# Revit family: NLRS_57_DUF_UN_round-tee-piece_LT_velu
name_source: partatom
category: Duct Fittings
units: mm (PartAtom-declared; Revit-internal decimal feet)

## family parameters
Always vertical = Yes
Cut with Voids When Loaded = No
OmniClass Number = 23.75.70.14.14
OmniClass Title = Couplings for Air Ductwork
Part Type = Tee
Round Connector Dimension = Use Diameter
Shared = No
Work Plane-Based = No

## types (1)
- ST
    Assembly Code = 57.00
    Default Elevation = 0 mm  [stored 0 ft]
    Description = Rond T-stuk
    IfcDescription = Rond T-stuk
    IfcExportAs = IfcDuctFittingType
    IfcExportType = TEE
    Manufacturer = Velu Klimaattechnische groothandel
    Model = Velu T-stuk
    NLRS_C_bestemming = Ventilatiesystemen
    NLRS_C_content_datum_gewijzigd = 01-12-2023
    NLRS_C_content_provider = Velu Klimaattechnische groothandel
    NLRS_C_content_versie = 3.21.02
    NLRS_C_description = Rond T-stuk
    Type Comments = Velu T-stuk
    Type Image = <None>
    URL = https://webshop.velu.nl
    VELU_Article_Data = ST
    VELU_Article_Data2 = VH

note: [stored X ft] marks values corroborated as IEEE doubles in the binary element streams (Revit-internal decimal feet)

## geometry (parser evidence)
native form markers: Sweep x6
no freeform markers — native parametric forms only
